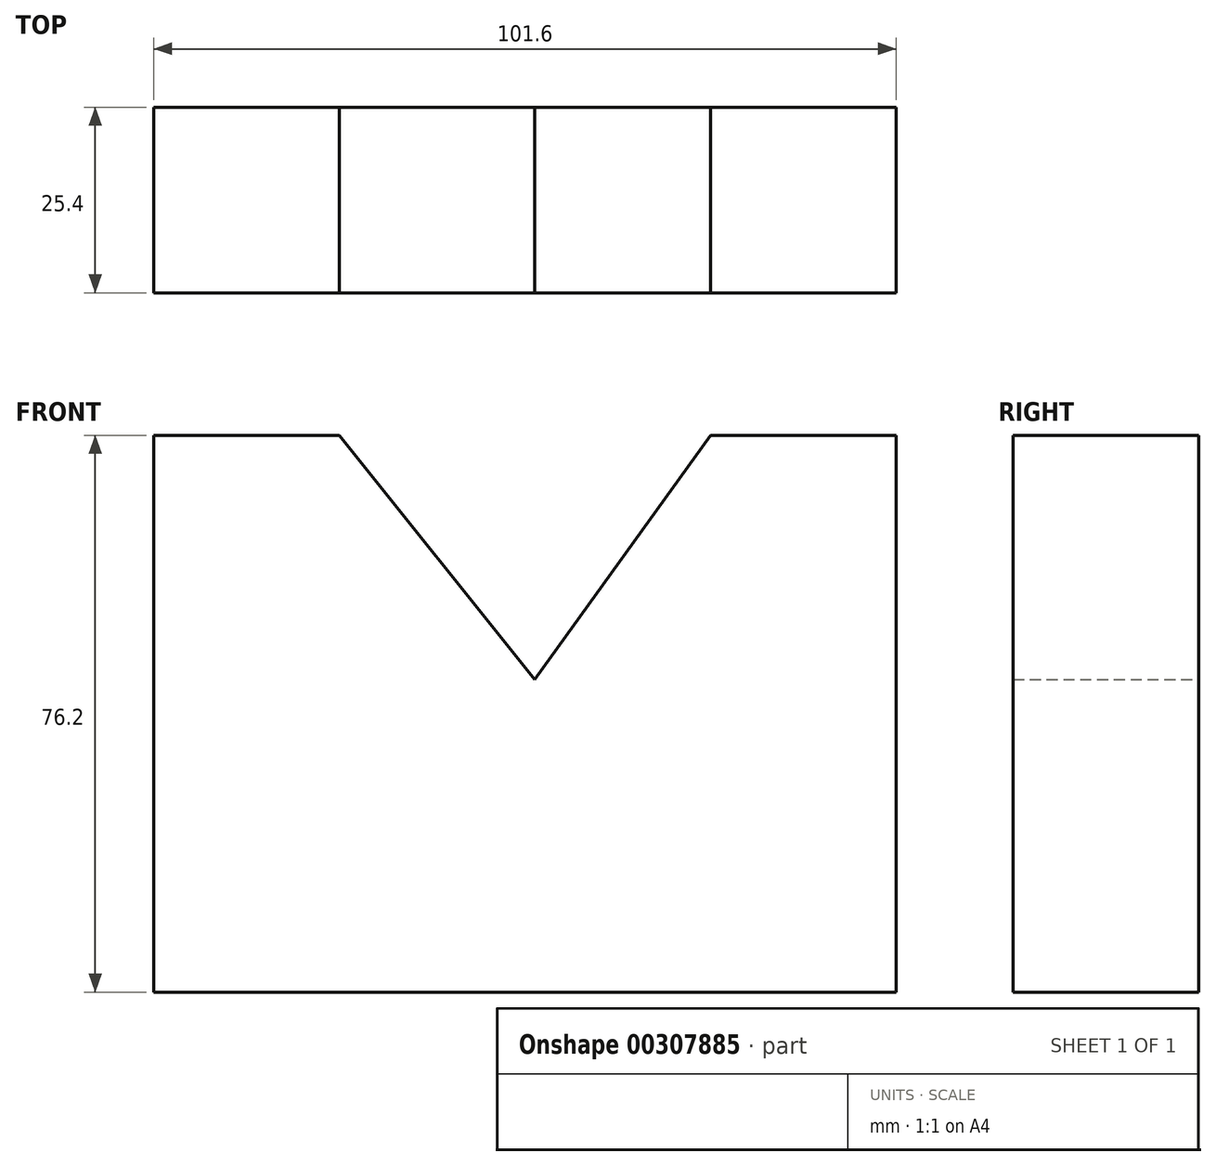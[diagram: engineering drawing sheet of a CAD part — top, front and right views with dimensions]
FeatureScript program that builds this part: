
annotation { "Feature Type Name" : "Feature", "Feature Type Description" : "" }
export const myFeature = defineFeature(function(context is Context, id is Id, definition is map)
    precondition{}
    {
        {
            var Q0;
            Q0=qCreatedBy(makeId("Front.planeOp"),FACE);
            var sketch = newSketch(context, id + "F0", { "sketchPlane" : qUnion([Q0])});
            skLineSegment(sketch, "E0", {"start": v(-54.18, -68.91) * mm, "end": v(47.42, -68.91) * mm});
            skLineSegment(sketch, "E1", {"start": v(47.42, -68.91) * mm, "end": v(47.42, 7.29) * mm});
            skLineSegment(sketch, "E2", {"start": v(-54.18, -68.91) * mm, "end": v(-54.18, 7.29) * mm});
            skLineSegment(sketch, "E3", {"start": v(-54.18, 7.29) * mm, "end": v(-28.78, 7.29) * mm});
            skLineSegment(sketch, "E4", {"start": v(47.42, 7.29) * mm, "end": v(22.02, 7.29) * mm});
            skLineSegment(sketch, "E5", {"start": v(-2.04, -26.13) * mm, "end": v(-28.78, 7.29) * mm});
            skLineSegment(sketch, "E6", {"start": v(-2.04, -26.13) * mm, "end": v(22.02, 7.29) * mm});
            skSolve(sketch);
        }
        {
            var Q0;
            Q0=makeQuery(id+"F0.imprint","IMPRINT",FACE,{"disambiguationData":[TD([[makeQuery(id+"F0.imprint","IMPRINT",EDGE,{"derivedFrom":sQuery(id+"F0.wireOp",EDGE,"E0")}),1.0]])]});
            extrude(context, id + "F1", {"entities" : qUnion([Q0]), "depth" : 25.4 * mm});
        }
    });
